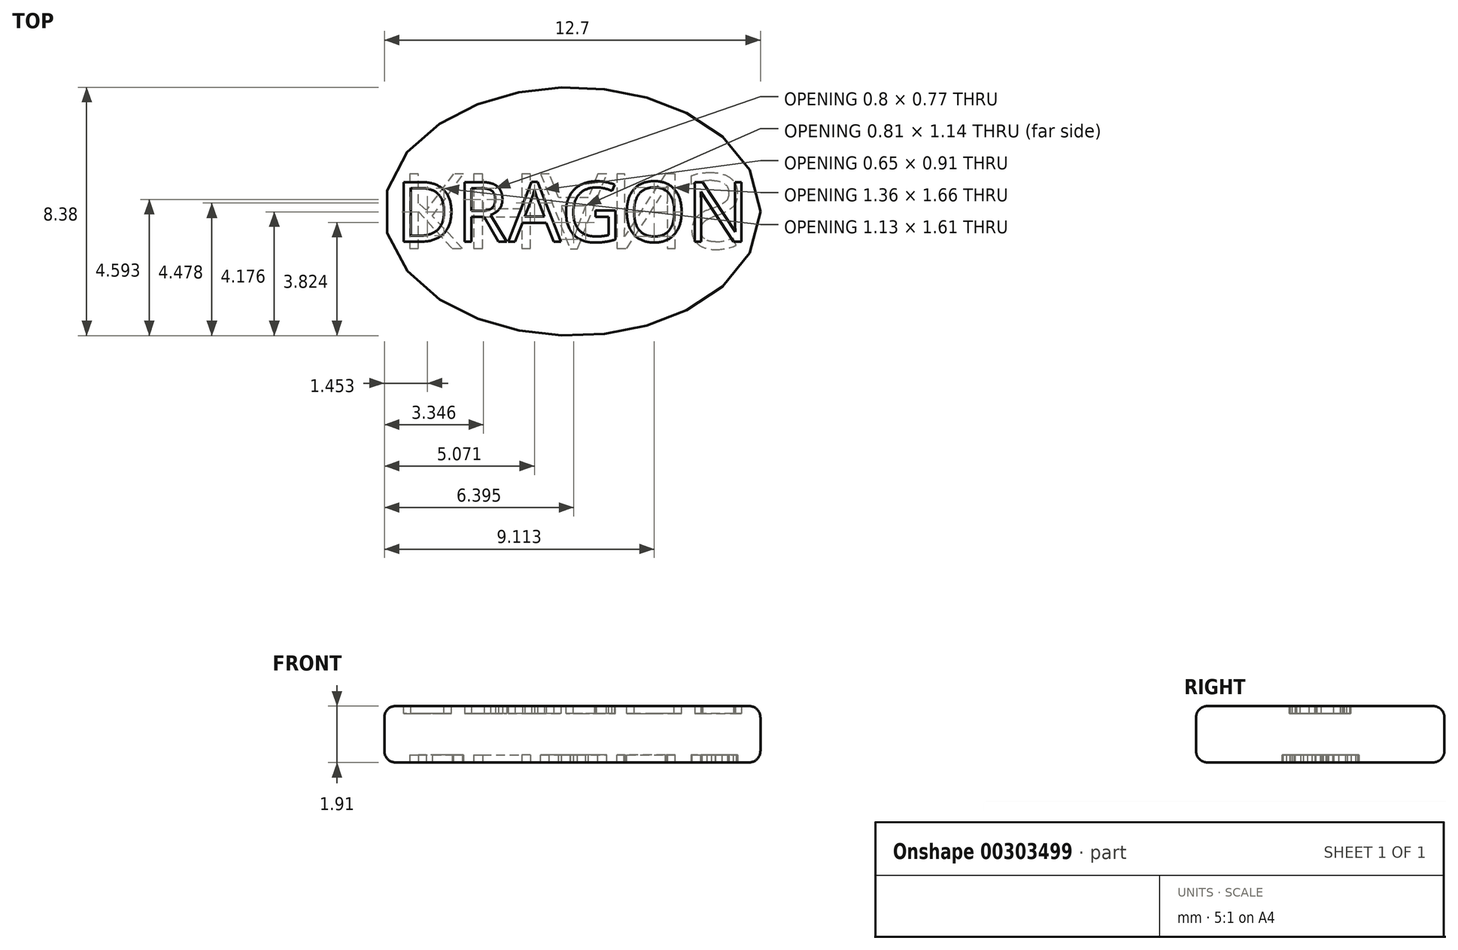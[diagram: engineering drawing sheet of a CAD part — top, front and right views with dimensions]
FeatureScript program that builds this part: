
annotation { "Feature Type Name" : "Feature", "Feature Type Description" : "" }
export const myFeature = defineFeature(function(context is Context, id is Id, definition is map)
    precondition{}
    {
        {
            var Q0;
            Q0=qCreatedBy(makeId("Top.planeOp"),FACE);
            var sketch = newSketch(context, id + "F0", { "sketchPlane" : qUnion([Q0])});
            skEllipse(sketch, "E0", {"center": v(0, 0) * mm, "majorRadius": 6.35 * mm, "minorRadius": 4.2 * mm, "majorAxis": v(1, 0)});
            skSolve(sketch);
        }
        {
            var Q0;
            Q0=qSketchRegion(id+"F0",true);
            extrude(context, id + "F1", {"entities" : qUnion([Q0]), "oppositeDirection" : true, "depth" : 1.9 * mm});
        }
        {
            var Q0;
            Q0=makeQuery(id+"F1.opExtrude","CAP_FACE",FACE,{"disambiguationData":[OSD([sQuery(id+"F0.wireOp",EDGE,"E0")])],"isStart":true});
            var sketch = newSketch(context, id + "F2", { "sketchPlane" : qUnion([Q0])});
            skEllipse(sketch, "E1.0", {"center": v(0, 0) * mm, "majorRadius": 6.35 * mm, "minorRadius": 4.2 * mm, "majorAxis": v(1, 0)});
            skLineSegment(sketch, "E2", {"start": v(0, 0) * mm, "end": v(5.9, 0) * mm, "construction": true});
            skLineSegment(sketch, "E3", {"start": v(5.9, 0) * mm, "end": v(5.9, -1.02) * mm, "construction": true});
            skLineSegment(sketch, "E4", {"start": v(5.9, 0) * mm, "end": v(5.9, 1.02) * mm, "construction": true});
            skText(sketch, "E5", { "text": "DRAGON", "fontName": "OpenSans-Regular.ttf"});
            const initialGuessF2  = {"E5": [-0.00597, -0.00102, 1, 0, 0.00203]};
            skSetInitialGuess(sketch, initialGuessF2);
            skSolve(sketch);
        }
        {
            var Q0;
            Q0=makeQuery(id+"F1.opExtrude","CAP_FACE",FACE,{"disambiguationData":[OSD([sQuery(id+"F0.wireOp",EDGE,"E0")])],"isStart":false});
            var sketch = newSketch(context, id + "F3", { "sketchPlane" : qUnion([Q0])});
            skEllipse(sketch, "E6.0", {"center": v(0, 0) * mm, "majorRadius": 6.35 * mm, "minorRadius": 4.2 * mm, "majorAxis": v(1, 0)});
            skLineSegment(sketch, "E7", {"start": v(0, 0) * mm, "end": v(-5.84, 0) * mm, "construction": true});
            skLineSegment(sketch, "E8", {"start": v(-5.84, 0) * mm, "end": v(-5.84, 1.27) * mm, "construction": true});
            skLineSegment(sketch, "E9", {"start": v(-5.84, 0) * mm, "end": v(-5.84, -1.27) * mm});
            skText(sketch, "E10", { "text": "KHANS", "fontName": "OpenSans-Regular.ttf"});
            const initialGuessF3  = {"E10": [-0.00584, -0.00127, 1, 0, 0.00254]};
            skSetInitialGuess(sketch, initialGuessF3);
            skSolve(sketch);
        }
        {
            var Q0;
            Q0=makeQuery(id+"F2.imprint","IMPRINT",FACE,{"disambiguationData":[TD([[makeQuery(id+"F2.imprint","IMPRINT",EDGE,{"derivedFrom":sQuery(id+"F2.wireOp",EDGE,"E5.sketch_text.stroke-0")}),-1.0]])]});
            var Q1;
            Q1=makeQuery(id+"F2.imprint","IMPRINT",FACE,{"disambiguationData":[TD([[makeQuery(id+"F2.imprint","IMPRINT",EDGE,{"derivedFrom":sQuery(id+"F2.wireOp",EDGE,"E5.sketch_text.stroke-14")}),-1.0]])]});
            var Q2;
            Q2=makeQuery(id+"F2.imprint","IMPRINT",FACE,{"disambiguationData":[TD([[makeQuery(id+"F2.imprint","IMPRINT",EDGE,{"derivedFrom":sQuery(id+"F2.wireOp",EDGE,"E5.sketch_text.stroke-32")}),-1.0]])]});
            var Q3;
            Q3=makeQuery(id+"F2.imprint","IMPRINT",FACE,{"disambiguationData":[TD([[makeQuery(id+"F2.imprint","IMPRINT",EDGE,{"derivedFrom":sQuery(id+"F2.wireOp",EDGE,"E5.sketch_text.stroke-45")}),-1.0]])]});
            var Q4;
            Q4=makeQuery(id+"F2.imprint","IMPRINT",FACE,{"disambiguationData":[TD([[makeQuery(id+"F2.imprint","IMPRINT",EDGE,{"derivedFrom":sQuery(id+"F2.wireOp",EDGE,"E5.sketch_text.stroke-65")}),-1.0]])]});
            var Q5;
            Q5=makeQuery(id+"F2.imprint","IMPRINT",FACE,{"disambiguationData":[TD([[makeQuery(id+"F2.imprint","IMPRINT",EDGE,{"derivedFrom":sQuery(id+"F2.wireOp",EDGE,"E5.sketch_text.stroke-81")}),-1.0]])]});
            extrude(context, id + "F4", {"entities" : qUnion([Q0, Q1, Q2, Q3, Q4, Q5]), "operationType" : NewBodyOperationType.REMOVE, "oppositeDirection" : true, "depth" : 0.25 * mm});
        }
        {
            var Q0;
            Q0=makeQuery(id+"F3.imprint","IMPRINT",FACE,{"disambiguationData":[TD([[makeQuery(id+"F3.imprint","IMPRINT",EDGE,{"derivedFrom":sQuery(id+"F3.wireOp",EDGE,"E10.sketch_text.stroke-0")}),-1.0]])]});
            var Q1;
            Q1=makeQuery(id+"F3.imprint","IMPRINT",FACE,{"disambiguationData":[TD([[makeQuery(id+"F3.imprint","IMPRINT",EDGE,{"derivedFrom":sQuery(id+"F3.wireOp",EDGE,"E10.sketch_text.stroke-12")}),-1.0]])]});
            var Q2;
            Q2=makeQuery(id+"F3.imprint","IMPRINT",FACE,{"disambiguationData":[TD([[makeQuery(id+"F3.imprint","IMPRINT",EDGE,{"derivedFrom":sQuery(id+"F3.wireOp",EDGE,"E10.sketch_text.stroke-24")}),-1.0]])]});
            var Q3;
            Q3=makeQuery(id+"F3.imprint","IMPRINT",FACE,{"disambiguationData":[TD([[makeQuery(id+"F3.imprint","IMPRINT",EDGE,{"derivedFrom":sQuery(id+"F3.wireOp",EDGE,"E10.sketch_text.stroke-37")}),-1.0]])]});
            var Q4;
            Q4=makeQuery(id+"F3.imprint","IMPRINT",FACE,{"disambiguationData":[TD([[makeQuery(id+"F3.imprint","IMPRINT",EDGE,{"derivedFrom":sQuery(id+"F3.wireOp",EDGE,"E10.sketch_text.stroke-52")}),-1.0]])]});
            extrude(context, id + "F5", {"entities" : qUnion([Q0, Q1, Q2, Q3, Q4]), "operationType" : NewBodyOperationType.REMOVE, "oppositeDirection" : true, "depth" : 0.25 * mm});
        }
        {
            var Q0;
            Q0=makeQuery(id+"F1.opExtrude","CAP_EDGE",EDGE,{"disambiguationData":[OSD([sQuery(id+"F0.wireOp",EDGE,"E0")])],"isStart":false});
            var Q1;
            Q1=makeQuery(id+"F1.opExtrude","CAP_EDGE",EDGE,{"disambiguationData":[OSD([sQuery(id+"F0.wireOp",EDGE,"E0")])],"isStart":true});
            fillet(context, id + "F6", {"entities" : qUnion([Q0, Q1]), "radius" : 0.38 * mm, "tangentPropagation" : true, "allowEdgeOverflow" : false});
        }
        {
            var Q0;
            Q0=makeQuery(id+"F4.boolean.opBoolean","COPY",FACE,{"derivedFrom":makeQuery(id+"F4.opExtrude","CAP_FACE",FACE,{"disambiguationData":[OSD([sQuery(id+"F2.wireOp",EDGE,"E5.sketch_text.stroke-0"),sQuery(id+"F2.wireOp",EDGE,"E5.sketch_text.stroke-1"),sQuery(id+"F2.wireOp",EDGE,"E5.sketch_text.stroke-2"),sQuery(id+"F2.wireOp",EDGE,"E5.sketch_text.stroke-3"),sQuery(id+"F2.wireOp",EDGE,"E5.sketch_text.stroke-4"),sQuery(id+"F2.wireOp",EDGE,"E5.sketch_text.stroke-5"),sQuery(id+"F2.wireOp",EDGE,"E5.sketch_text.stroke-6"),sQuery(id+"F2.wireOp",EDGE,"E5.sketch_text.stroke-7"),sQuery(id+"F2.wireOp",EDGE,"E5.sketch_text.stroke-8"),sQuery(id+"F2.wireOp",EDGE,"E5.sketch_text.stroke-9"),sQuery(id+"F2.wireOp",EDGE,"E5.sketch_text.stroke-10"),sQuery(id+"F2.wireOp",EDGE,"E5.sketch_text.stroke-11"),sQuery(id+"F2.wireOp",EDGE,"E5.sketch_text.stroke-12"),sQuery(id+"F2.wireOp",EDGE,"E5.sketch_text.stroke-13")])],"isStart":false})});
            var Q1;
            Q1=makeQuery(id+"F4.boolean.opBoolean","COPY",FACE,{"derivedFrom":makeQuery(id+"F4.opExtrude","CAP_FACE",FACE,{"disambiguationData":[OSD([sQuery(id+"F2.wireOp",EDGE,"E5.sketch_text.stroke-14"),sQuery(id+"F2.wireOp",EDGE,"E5.sketch_text.stroke-15"),sQuery(id+"F2.wireOp",EDGE,"E5.sketch_text.stroke-16"),sQuery(id+"F2.wireOp",EDGE,"E5.sketch_text.stroke-17"),sQuery(id+"F2.wireOp",EDGE,"E5.sketch_text.stroke-18"),sQuery(id+"F2.wireOp",EDGE,"E5.sketch_text.stroke-19"),sQuery(id+"F2.wireOp",EDGE,"E5.sketch_text.stroke-20"),sQuery(id+"F2.wireOp",EDGE,"E5.sketch_text.stroke-21"),sQuery(id+"F2.wireOp",EDGE,"E5.sketch_text.stroke-22"),sQuery(id+"F2.wireOp",EDGE,"E5.sketch_text.stroke-23"),sQuery(id+"F2.wireOp",EDGE,"E5.sketch_text.stroke-24"),sQuery(id+"F2.wireOp",EDGE,"E5.sketch_text.stroke-25"),sQuery(id+"F2.wireOp",EDGE,"E5.sketch_text.stroke-26"),sQuery(id+"F2.wireOp",EDGE,"E5.sketch_text.stroke-27"),sQuery(id+"F2.wireOp",EDGE,"E5.sketch_text.stroke-28"),sQuery(id+"F2.wireOp",EDGE,"E5.sketch_text.stroke-29"),sQuery(id+"F2.wireOp",EDGE,"E5.sketch_text.stroke-30"),sQuery(id+"F2.wireOp",EDGE,"E5.sketch_text.stroke-31")])],"isStart":false})});
            var Q2;
            Q2=makeQuery(id+"F4.boolean.opBoolean","COPY",FACE,{"derivedFrom":makeQuery(id+"F4.opExtrude","CAP_FACE",FACE,{"disambiguationData":[OSD([sQuery(id+"F2.wireOp",EDGE,"E5.sketch_text.stroke-32"),sQuery(id+"F2.wireOp",EDGE,"E5.sketch_text.stroke-33"),sQuery(id+"F2.wireOp",EDGE,"E5.sketch_text.stroke-34"),sQuery(id+"F2.wireOp",EDGE,"E5.sketch_text.stroke-35"),sQuery(id+"F2.wireOp",EDGE,"E5.sketch_text.stroke-36"),sQuery(id+"F2.wireOp",EDGE,"E5.sketch_text.stroke-37"),sQuery(id+"F2.wireOp",EDGE,"E5.sketch_text.stroke-38"),sQuery(id+"F2.wireOp",EDGE,"E5.sketch_text.stroke-39"),sQuery(id+"F2.wireOp",EDGE,"E5.sketch_text.stroke-40"),sQuery(id+"F2.wireOp",EDGE,"E5.sketch_text.stroke-41"),sQuery(id+"F2.wireOp",EDGE,"E5.sketch_text.stroke-42"),sQuery(id+"F2.wireOp",EDGE,"E5.sketch_text.stroke-43"),sQuery(id+"F2.wireOp",EDGE,"E5.sketch_text.stroke-44")])],"isStart":false})});
            var Q3;
            Q3=makeQuery(id+"F4.boolean.opBoolean","COPY",FACE,{"derivedFrom":makeQuery(id+"F4.opExtrude","CAP_FACE",FACE,{"disambiguationData":[OSD([sQuery(id+"F2.wireOp",EDGE,"E5.sketch_text.stroke-45"),sQuery(id+"F2.wireOp",EDGE,"E5.sketch_text.stroke-46"),sQuery(id+"F2.wireOp",EDGE,"E5.sketch_text.stroke-47"),sQuery(id+"F2.wireOp",EDGE,"E5.sketch_text.stroke-48"),sQuery(id+"F2.wireOp",EDGE,"E5.sketch_text.stroke-49"),sQuery(id+"F2.wireOp",EDGE,"E5.sketch_text.stroke-50"),sQuery(id+"F2.wireOp",EDGE,"E5.sketch_text.stroke-51"),sQuery(id+"F2.wireOp",EDGE,"E5.sketch_text.stroke-52"),sQuery(id+"F2.wireOp",EDGE,"E5.sketch_text.stroke-53"),sQuery(id+"F2.wireOp",EDGE,"E5.sketch_text.stroke-54"),sQuery(id+"F2.wireOp",EDGE,"E5.sketch_text.stroke-55"),sQuery(id+"F2.wireOp",EDGE,"E5.sketch_text.stroke-56"),sQuery(id+"F2.wireOp",EDGE,"E5.sketch_text.stroke-57"),sQuery(id+"F2.wireOp",EDGE,"E5.sketch_text.stroke-58"),sQuery(id+"F2.wireOp",EDGE,"E5.sketch_text.stroke-59"),sQuery(id+"F2.wireOp",EDGE,"E5.sketch_text.stroke-60"),sQuery(id+"F2.wireOp",EDGE,"E5.sketch_text.stroke-61"),sQuery(id+"F2.wireOp",EDGE,"E5.sketch_text.stroke-62"),sQuery(id+"F2.wireOp",EDGE,"E5.sketch_text.stroke-63"),sQuery(id+"F2.wireOp",EDGE,"E5.sketch_text.stroke-64")])],"isStart":false})});
            var Q4;
            Q4=makeQuery(id+"F4.boolean.opBoolean","COPY",FACE,{"derivedFrom":makeQuery(id+"F4.opExtrude","CAP_FACE",FACE,{"disambiguationData":[OSD([sQuery(id+"F2.wireOp",EDGE,"E5.sketch_text.stroke-65"),sQuery(id+"F2.wireOp",EDGE,"E5.sketch_text.stroke-66"),sQuery(id+"F2.wireOp",EDGE,"E5.sketch_text.stroke-67"),sQuery(id+"F2.wireOp",EDGE,"E5.sketch_text.stroke-68"),sQuery(id+"F2.wireOp",EDGE,"E5.sketch_text.stroke-69"),sQuery(id+"F2.wireOp",EDGE,"E5.sketch_text.stroke-70"),sQuery(id+"F2.wireOp",EDGE,"E5.sketch_text.stroke-71"),sQuery(id+"F2.wireOp",EDGE,"E5.sketch_text.stroke-72"),sQuery(id+"F2.wireOp",EDGE,"E5.sketch_text.stroke-73"),sQuery(id+"F2.wireOp",EDGE,"E5.sketch_text.stroke-74"),sQuery(id+"F2.wireOp",EDGE,"E5.sketch_text.stroke-75"),sQuery(id+"F2.wireOp",EDGE,"E5.sketch_text.stroke-76"),sQuery(id+"F2.wireOp",EDGE,"E5.sketch_text.stroke-77"),sQuery(id+"F2.wireOp",EDGE,"E5.sketch_text.stroke-78"),sQuery(id+"F2.wireOp",EDGE,"E5.sketch_text.stroke-79"),sQuery(id+"F2.wireOp",EDGE,"E5.sketch_text.stroke-80")])],"isStart":false})});
            var Q5;
            Q5=makeQuery(id+"F4.boolean.opBoolean","COPY",FACE,{"derivedFrom":makeQuery(id+"F4.opExtrude","CAP_FACE",FACE,{"disambiguationData":[OSD([sQuery(id+"F2.wireOp",EDGE,"E5.sketch_text.stroke-81"),sQuery(id+"F2.wireOp",EDGE,"E5.sketch_text.stroke-82"),sQuery(id+"F2.wireOp",EDGE,"E5.sketch_text.stroke-83"),sQuery(id+"F2.wireOp",EDGE,"E5.sketch_text.stroke-84"),sQuery(id+"F2.wireOp",EDGE,"E5.sketch_text.stroke-85"),sQuery(id+"F2.wireOp",EDGE,"E5.sketch_text.stroke-86"),sQuery(id+"F2.wireOp",EDGE,"E5.sketch_text.stroke-87"),sQuery(id+"F2.wireOp",EDGE,"E5.sketch_text.stroke-88"),sQuery(id+"F2.wireOp",EDGE,"E5.sketch_text.stroke-89"),sQuery(id+"F2.wireOp",EDGE,"E5.sketch_text.stroke-90"),sQuery(id+"F2.wireOp",EDGE,"E5.sketch_text.stroke-91"),sQuery(id+"F2.wireOp",EDGE,"E5.sketch_text.stroke-92"),sQuery(id+"F2.wireOp",EDGE,"E5.sketch_text.stroke-93"),sQuery(id+"F2.wireOp",EDGE,"E5.sketch_text.stroke-94"),sQuery(id+"F2.wireOp",EDGE,"E5.sketch_text.stroke-95")])],"isStart":false})});
            extrude(context, id + "F7", {"entities" : qUnion([Q0, Q1, Q2, Q3, Q4, Q5]), "depth" : 0.25 * mm});
        }
        {
            var Q0;
            Q0=makeQuery(id+"F5.boolean.opBoolean","COPY",FACE,{"derivedFrom":makeQuery(id+"F5.opExtrude","CAP_FACE",FACE,{"disambiguationData":[OSD([sQuery(id+"F3.wireOp",EDGE,"E10.sketch_text.stroke-0"),sQuery(id+"F3.wireOp",EDGE,"E10.sketch_text.stroke-1"),sQuery(id+"F3.wireOp",EDGE,"E10.sketch_text.stroke-2"),sQuery(id+"F3.wireOp",EDGE,"E10.sketch_text.stroke-3"),sQuery(id+"F3.wireOp",EDGE,"E10.sketch_text.stroke-4"),sQuery(id+"F3.wireOp",EDGE,"E10.sketch_text.stroke-5"),sQuery(id+"F3.wireOp",EDGE,"E10.sketch_text.stroke-6"),sQuery(id+"F3.wireOp",EDGE,"E10.sketch_text.stroke-7"),sQuery(id+"F3.wireOp",EDGE,"E10.sketch_text.stroke-8"),sQuery(id+"F3.wireOp",EDGE,"E10.sketch_text.stroke-9"),sQuery(id+"F3.wireOp",EDGE,"E10.sketch_text.stroke-10"),sQuery(id+"F3.wireOp",EDGE,"E10.sketch_text.stroke-11")])],"isStart":false})});
            var Q1;
            Q1=makeQuery(id+"F5.boolean.opBoolean","COPY",FACE,{"derivedFrom":makeQuery(id+"F5.opExtrude","CAP_FACE",FACE,{"disambiguationData":[OSD([sQuery(id+"F3.wireOp",EDGE,"E10.sketch_text.stroke-12"),sQuery(id+"F3.wireOp",EDGE,"E10.sketch_text.stroke-13"),sQuery(id+"F3.wireOp",EDGE,"E10.sketch_text.stroke-14"),sQuery(id+"F3.wireOp",EDGE,"E10.sketch_text.stroke-15"),sQuery(id+"F3.wireOp",EDGE,"E10.sketch_text.stroke-16"),sQuery(id+"F3.wireOp",EDGE,"E10.sketch_text.stroke-17"),sQuery(id+"F3.wireOp",EDGE,"E10.sketch_text.stroke-18"),sQuery(id+"F3.wireOp",EDGE,"E10.sketch_text.stroke-19"),sQuery(id+"F3.wireOp",EDGE,"E10.sketch_text.stroke-20"),sQuery(id+"F3.wireOp",EDGE,"E10.sketch_text.stroke-21"),sQuery(id+"F3.wireOp",EDGE,"E10.sketch_text.stroke-22"),sQuery(id+"F3.wireOp",EDGE,"E10.sketch_text.stroke-23")])],"isStart":false})});
            var Q2;
            Q2=makeQuery(id+"F5.boolean.opBoolean","COPY",FACE,{"derivedFrom":makeQuery(id+"F5.opExtrude","CAP_FACE",FACE,{"disambiguationData":[OSD([sQuery(id+"F3.wireOp",EDGE,"E10.sketch_text.stroke-24"),sQuery(id+"F3.wireOp",EDGE,"E10.sketch_text.stroke-25"),sQuery(id+"F3.wireOp",EDGE,"E10.sketch_text.stroke-26"),sQuery(id+"F3.wireOp",EDGE,"E10.sketch_text.stroke-27"),sQuery(id+"F3.wireOp",EDGE,"E10.sketch_text.stroke-28"),sQuery(id+"F3.wireOp",EDGE,"E10.sketch_text.stroke-29"),sQuery(id+"F3.wireOp",EDGE,"E10.sketch_text.stroke-30"),sQuery(id+"F3.wireOp",EDGE,"E10.sketch_text.stroke-31"),sQuery(id+"F3.wireOp",EDGE,"E10.sketch_text.stroke-32"),sQuery(id+"F3.wireOp",EDGE,"E10.sketch_text.stroke-33"),sQuery(id+"F3.wireOp",EDGE,"E10.sketch_text.stroke-34"),sQuery(id+"F3.wireOp",EDGE,"E10.sketch_text.stroke-35"),sQuery(id+"F3.wireOp",EDGE,"E10.sketch_text.stroke-36")])],"isStart":false})});
            var Q3;
            Q3=makeQuery(id+"F5.boolean.opBoolean","COPY",FACE,{"derivedFrom":makeQuery(id+"F5.opExtrude","CAP_FACE",FACE,{"disambiguationData":[OSD([sQuery(id+"F3.wireOp",EDGE,"E10.sketch_text.stroke-37"),sQuery(id+"F3.wireOp",EDGE,"E10.sketch_text.stroke-38"),sQuery(id+"F3.wireOp",EDGE,"E10.sketch_text.stroke-39"),sQuery(id+"F3.wireOp",EDGE,"E10.sketch_text.stroke-40"),sQuery(id+"F3.wireOp",EDGE,"E10.sketch_text.stroke-41"),sQuery(id+"F3.wireOp",EDGE,"E10.sketch_text.stroke-42"),sQuery(id+"F3.wireOp",EDGE,"E10.sketch_text.stroke-43"),sQuery(id+"F3.wireOp",EDGE,"E10.sketch_text.stroke-44"),sQuery(id+"F3.wireOp",EDGE,"E10.sketch_text.stroke-45"),sQuery(id+"F3.wireOp",EDGE,"E10.sketch_text.stroke-46"),sQuery(id+"F3.wireOp",EDGE,"E10.sketch_text.stroke-47"),sQuery(id+"F3.wireOp",EDGE,"E10.sketch_text.stroke-48"),sQuery(id+"F3.wireOp",EDGE,"E10.sketch_text.stroke-49"),sQuery(id+"F3.wireOp",EDGE,"E10.sketch_text.stroke-50"),sQuery(id+"F3.wireOp",EDGE,"E10.sketch_text.stroke-51")])],"isStart":false})});
            var Q4;
            Q4=makeQuery(id+"F5.boolean.opBoolean","COPY",FACE,{"derivedFrom":makeQuery(id+"F5.opExtrude","CAP_FACE",FACE,{"disambiguationData":[OSD([sQuery(id+"F3.wireOp",EDGE,"E10.sketch_text.stroke-52"),sQuery(id+"F3.wireOp",EDGE,"E10.sketch_text.stroke-53"),sQuery(id+"F3.wireOp",EDGE,"E10.sketch_text.stroke-54"),sQuery(id+"F3.wireOp",EDGE,"E10.sketch_text.stroke-55"),sQuery(id+"F3.wireOp",EDGE,"E10.sketch_text.stroke-56"),sQuery(id+"F3.wireOp",EDGE,"E10.sketch_text.stroke-57"),sQuery(id+"F3.wireOp",EDGE,"E10.sketch_text.stroke-58"),sQuery(id+"F3.wireOp",EDGE,"E10.sketch_text.stroke-59"),sQuery(id+"F3.wireOp",EDGE,"E10.sketch_text.stroke-60"),sQuery(id+"F3.wireOp",EDGE,"E10.sketch_text.stroke-61"),sQuery(id+"F3.wireOp",EDGE,"E10.sketch_text.stroke-62"),sQuery(id+"F3.wireOp",EDGE,"E10.sketch_text.stroke-63"),sQuery(id+"F3.wireOp",EDGE,"E10.sketch_text.stroke-64"),sQuery(id+"F3.wireOp",EDGE,"E10.sketch_text.stroke-65"),sQuery(id+"F3.wireOp",EDGE,"E10.sketch_text.stroke-66"),sQuery(id+"F3.wireOp",EDGE,"E10.sketch_text.stroke-67"),sQuery(id+"F3.wireOp",EDGE,"E10.sketch_text.stroke-68"),sQuery(id+"F3.wireOp",EDGE,"E10.sketch_text.stroke-69"),sQuery(id+"F3.wireOp",EDGE,"E10.sketch_text.stroke-70"),sQuery(id+"F3.wireOp",EDGE,"E10.sketch_text.stroke-71"),sQuery(id+"F3.wireOp",EDGE,"E10.sketch_text.stroke-72"),sQuery(id+"F3.wireOp",EDGE,"E10.sketch_text.stroke-73"),sQuery(id+"F3.wireOp",EDGE,"E10.sketch_text.stroke-74"),sQuery(id+"F3.wireOp",EDGE,"E10.sketch_text.stroke-75"),sQuery(id+"F3.wireOp",EDGE,"E10.sketch_text.stroke-76")])],"isStart":false})});
            extrude(context, id + "F8", {"entities" : qUnion([Q0, Q1, Q2, Q3, Q4]), "depth" : 0.25 * mm});
        }
    });
